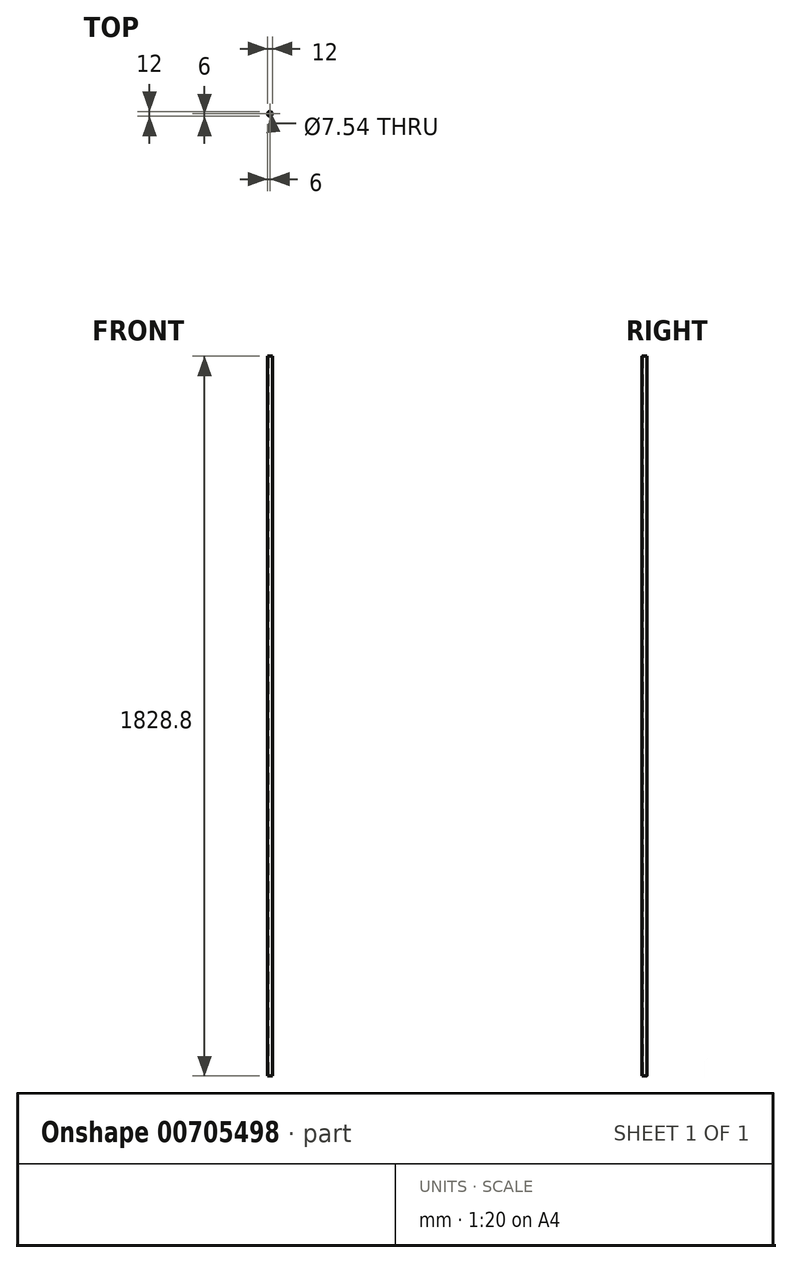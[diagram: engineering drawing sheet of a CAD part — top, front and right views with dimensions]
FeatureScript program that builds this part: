
annotation { "Feature Type Name" : "Feature", "Feature Type Description" : "" }
export const myFeature = defineFeature(function(context is Context, id is Id, definition is map)
    precondition{}
    {
        {
            var Q0;
            Q0=qCreatedBy(makeId("Top.planeOp"),FACE);
            var sketch = newSketch(context, id + "F0", { "sketchPlane" : qUnion([Q0])});
            skCircle(sketch, "E0", {"center": v(0, 0) * mm, "radius": 6 * mm});
            skCircle(sketch, "E1", {"center": v(0, 0) * mm, "radius": 3.77 * mm});
            skSolve(sketch);
        }
        {
            var Q0;
            Q0 = qSketchRegion(id + "F0", true);
            extrude(context, id + "F1", {"entities" : qUnion([Q0]), "depth" : 1828.8 * mm, "offsetDistance" : 25.4 * mm});
        }
    });
